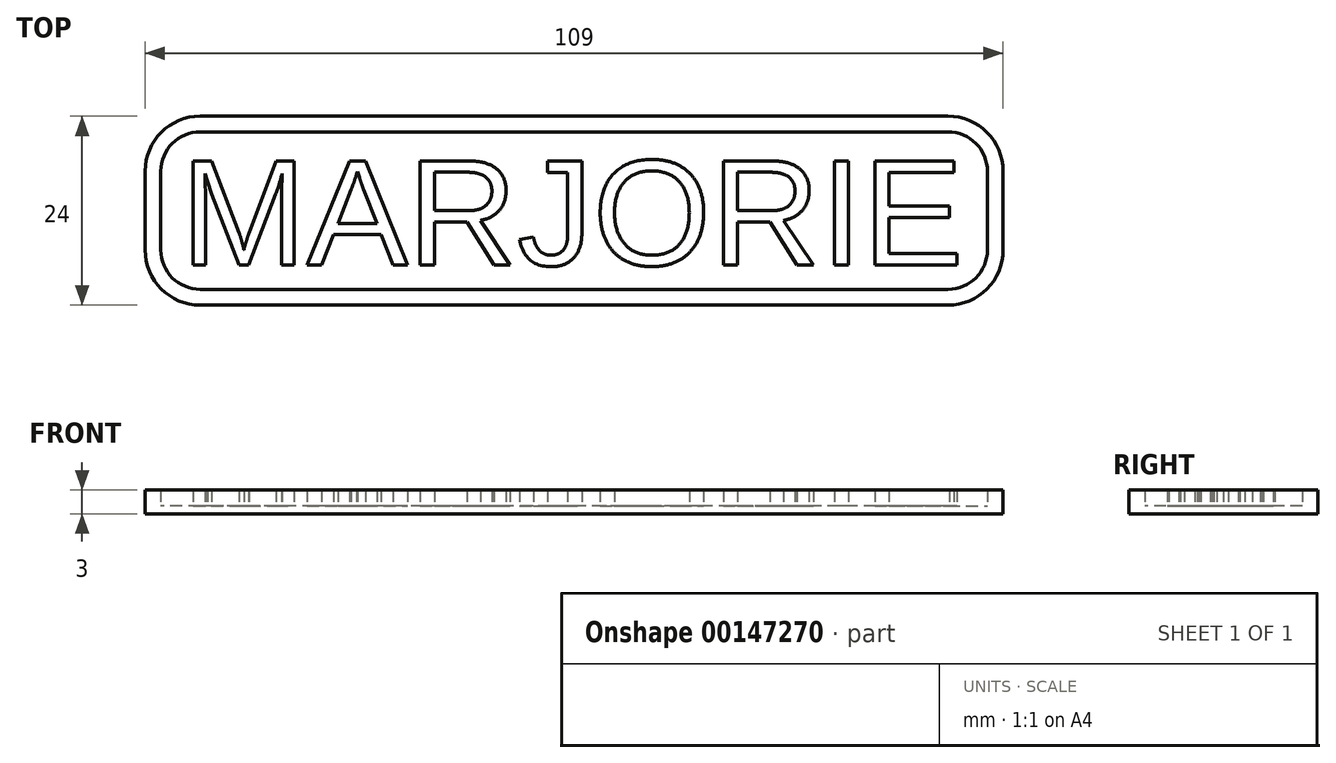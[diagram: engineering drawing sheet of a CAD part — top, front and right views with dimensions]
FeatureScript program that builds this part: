
annotation { "Feature Type Name" : "Feature", "Feature Type Description" : "" }
export const myFeature = defineFeature(function(context is Context, id is Id, definition is map)
    precondition{}
    {
        {
            var Q0;
            Q0=qCreatedBy(makeId("Top.planeOp"),FACE);
            var sketch = newSketch(context, id + "F0", { "sketchPlane" : qUnion([Q0])});
            skText(sketch, "E0", { "text": "MARJORIE", "fontName": "Arimo-Regular.ttf"});
            skLineSegment(sketch, "E1.bottom", {"start": v(47.5, -3.07) * mm, "end": v(-47.5, -3.07) * mm});
            skLineSegment(sketch, "E1.top", {"start": v(47.5, 16.93) * mm, "end": v(-47.5, 16.93) * mm});
            skLineSegment(sketch, "E1.left", {"start": v(52.5, 1.93) * mm, "end": v(52.5, 11.93) * mm});
            skLineSegment(sketch, "E1.right", {"start": v(-52.5, 1.93) * mm, "end": v(-52.5, 11.93) * mm});
            skPoint(sketch, "E1.middle", {"position": v(0, 6.93) * mm});
            skPoint(sketch, "E2.visualSharp", {"position": v(-52.5, 16.93) * mm});
            skArc(sketch, "E2.filletArc", {"start": v(-47.5, 16.93) * mm, "mid": v(-51.04, 15.47) * mm, "end": v(-52.5, 11.93) * mm});
            skPoint(sketch, "E3.visualSharp", {"position": v(-52.5, -3.07) * mm});
            skArc(sketch, "E3.filletArc", {"start": v(-52.5, 1.93) * mm, "mid": v(-51.04, -1.6) * mm, "end": v(-47.5, -3.07) * mm});
            skPoint(sketch, "E4.visualSharp", {"position": v(52.5, 16.93) * mm});
            skArc(sketch, "E4.filletArc", {"start": v(52.5, 11.93) * mm, "mid": v(51.04, 15.47) * mm, "end": v(47.5, 16.93) * mm});
            skPoint(sketch, "E5.visualSharp", {"position": v(52.5, -3.07) * mm});
            skArc(sketch, "E5.filletArc", {"start": v(47.5, -3.07) * mm, "mid": v(51.04, -1.6) * mm, "end": v(52.5, 1.93) * mm});
            skArc(sketch, "E6.0", {"start": v(54.5, 11.93) * mm, "mid": v(52.45, 16.88) * mm, "end": v(47.5, 18.93) * mm});
            skLineSegment(sketch, "E6.1", {"start": v(54.5, 1.93) * mm, "end": v(54.5, 11.93) * mm});
            skLineSegment(sketch, "E6.2", {"start": v(47.5, 18.93) * mm, "end": v(-47.5, 18.93) * mm});
            skArc(sketch, "E6.3", {"start": v(47.5, -5.07) * mm, "mid": v(52.45, -3.02) * mm, "end": v(54.5, 1.93) * mm});
            skArc(sketch, "E6.4", {"start": v(-47.5, 18.93) * mm, "mid": v(-52.45, 16.88) * mm, "end": v(-54.5, 11.93) * mm});
            skLineSegment(sketch, "E6.5", {"start": v(-54.5, 1.93) * mm, "end": v(-54.5, 11.93) * mm});
            skArc(sketch, "E6.6", {"start": v(-54.5, 1.93) * mm, "mid": v(-52.45, -3.02) * mm, "end": v(-47.5, -5.07) * mm});
            skLineSegment(sketch, "E6.7", {"start": v(47.5, -5.07) * mm, "end": v(-47.5, -5.07) * mm});
            const initialGuessF0  = {"E0": [-0.05, 0, 1, 0, 0.01386]};
            skSetInitialGuess(sketch, initialGuessF0);
            skSolve(sketch);
        }
        {
            var Q0;
            Q0=makeQuery(id+"F0.imprint","IMPRINT",FACE,{"disambiguationData":[TD([[makeQuery(id+"F0.imprint","IMPRINT",EDGE,{"derivedFrom":sQuery(id+"F0.wireOp",EDGE,"E0.sketch_text.stroke-0")}),-1.0]])]});
            var Q1;
            Q1=makeQuery(id+"F0.imprint","IMPRINT",FACE,{"disambiguationData":[TD([[makeQuery(id+"F0.imprint","IMPRINT",EDGE,{"derivedFrom":sQuery(id+"F0.wireOp",EDGE,"E0.sketch_text.stroke-23")}),-1.0]])]});
            var Q2;
            Q2=makeQuery(id+"F0.imprint","IMPRINT",FACE,{"disambiguationData":[TD([[makeQuery(id+"F0.imprint","IMPRINT",EDGE,{"derivedFrom":sQuery(id+"F0.wireOp",EDGE,"E0.sketch_text.stroke-38")}),-1.0]])]});
            var Q3;
            Q3=makeQuery(id+"F0.imprint","IMPRINT",FACE,{"disambiguationData":[TD([[makeQuery(id+"F0.imprint","IMPRINT",EDGE,{"derivedFrom":sQuery(id+"F0.wireOp",EDGE,"E0.sketch_text.stroke-57")}),-1.0]])]});
            var Q4;
            Q4=makeQuery(id+"F0.imprint","IMPRINT",FACE,{"disambiguationData":[TD([[makeQuery(id+"F0.imprint","IMPRINT",EDGE,{"derivedFrom":sQuery(id+"F0.wireOp",EDGE,"E0.sketch_text.stroke-70")}),-1.0]])]});
            var Q5;
            Q5=makeQuery(id+"F0.imprint","IMPRINT",FACE,{"disambiguationData":[TD([[makeQuery(id+"F0.imprint","IMPRINT",EDGE,{"derivedFrom":sQuery(id+"F0.wireOp",EDGE,"E0.sketch_text.stroke-89")}),-1.0]])]});
            var Q6;
            Q6=makeQuery(id+"F0.imprint","IMPRINT",FACE,{"disambiguationData":[TD([[makeQuery(id+"F0.imprint","IMPRINT",EDGE,{"derivedFrom":sQuery(id+"F0.wireOp",EDGE,"E0.sketch_text.stroke-108")}),-1.0]])]});
            var Q7;
            Q7=makeQuery(id+"F0.imprint","IMPRINT",FACE,{"disambiguationData":[TD([[makeQuery(id+"F0.imprint","IMPRINT",EDGE,{"derivedFrom":sQuery(id+"F0.wireOp",EDGE,"E0.sketch_text.stroke-112")}),-1.0]])]});
            var Q8;
            Q8=makeQuery(id+"F0.imprint","IMPRINT",FACE,{"disambiguationData":[TD([[makeQuery(id+"F0.imprint","IMPRINT",EDGE,{"derivedFrom":sQuery(id+"F0.wireOp",EDGE,"E1.bottom")}),1.0]])]});
            extrude(context, id + "F1", {"entities" : qUnion([Q0, Q1, Q2, Q3, Q4, Q5, Q6, Q7, Q8]), "depth" : 3 * mm});
        }
        {
            var Q0;
            Q0=qCreatedBy(makeId("Top.planeOp"),FACE);
            var sketch = newSketch(context, id + "F2", { "sketchPlane" : qUnion([Q0])});
            skLineSegment(sketch, "E7.0", {"start": v(47.5, 18.93) * mm, "end": v(-47.5, 18.93) * mm});
            skArc(sketch, "E7.1", {"start": v(54.5, 11.93) * mm, "mid": v(52.45, 16.88) * mm, "end": v(47.5, 18.93) * mm});
            skLineSegment(sketch, "E7.2", {"start": v(54.5, 1.93) * mm, "end": v(54.5, 11.93) * mm});
            skArc(sketch, "E7.3", {"start": v(47.5, -5.07) * mm, "mid": v(52.45, -3.02) * mm, "end": v(54.5, 1.93) * mm});
            skLineSegment(sketch, "E7.4", {"start": v(47.5, -5.07) * mm, "end": v(-47.5, -5.07) * mm});
            skArc(sketch, "E7.5", {"start": v(-54.5, 1.93) * mm, "mid": v(-52.45, -3.02) * mm, "end": v(-47.5, -5.07) * mm});
            skLineSegment(sketch, "E7.6", {"start": v(-54.5, 1.93) * mm, "end": v(-54.5, 11.93) * mm});
            skArc(sketch, "E7.7", {"start": v(-47.5, 18.93) * mm, "mid": v(-52.45, 16.88) * mm, "end": v(-54.5, 11.93) * mm});
            skSolve(sketch);
        }
        {
            var Q0;
            Q0 = qSketchRegion(id + "F2", true);
            extrude(context, id + "F3", {"entities" : qUnion([Q0]), "operationType" : NewBodyOperationType.ADD, "depth" : 1 * mm});
        }
    });
